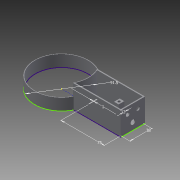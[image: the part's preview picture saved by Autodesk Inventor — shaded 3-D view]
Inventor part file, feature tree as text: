
AUTODESK INVENTOR PART (.ipt)
format: ipt  version: 2013 SP2 (Build 170200200, 200)  size: 158,208 bytes
history: native  units: mm
features: extrude x6, sketch x4, projected_geometry x2
ambient origin geometry x8: Origin, YZ Plane, XZ Plane, XY Plane, X Axis, Y Axis, Z Axis, Center Point
bodies: Solid1 (feature_tree)
feature tree (12):
  sketch  "Sketch1"  dims[d0=91.5mm d2=1.0mm]
  extrude  "Extrusion1"  Depth=1.0mm
  extrude  "Extrusion2"  Depth=38.0mm
  extrude  "Extrusion9"  Depth=20.0mm TaperAngle=0.0deg
  extrude  "Extrusion10"  Depth=40.0mm TaperAngle=0.0deg
  extrude  "Extrusion11"  Depth=8.1mm
  extrude  "Extrusion12"  Depth=12.0mm
  sketch  "Sketch8"  dims[d3=75.0mm d4=38.0mm]
  sketch  "Sketch9"  dims[d5=2.0mm d6=20.0mm d7=0.0mm]
  sketch  "Sketch10"  dims[d8=2.0mm d9=0.0mm d38=40.0mm d39=0.0mm d40=8.1mm d42=12.0mm d43=6.5mm d44=12.0mm d45=0.0mm d46=0.0mm d49=35.0mm d52=18.5mm d53=8.0mm d54=15.0mm d55=0.0mm d56=5.0mm d57=0.0mm d58=4.2mm d61=18.0mm]
  projected_geometry  "Projected Loop6"
  projected_geometry  "Projected Loop7"
